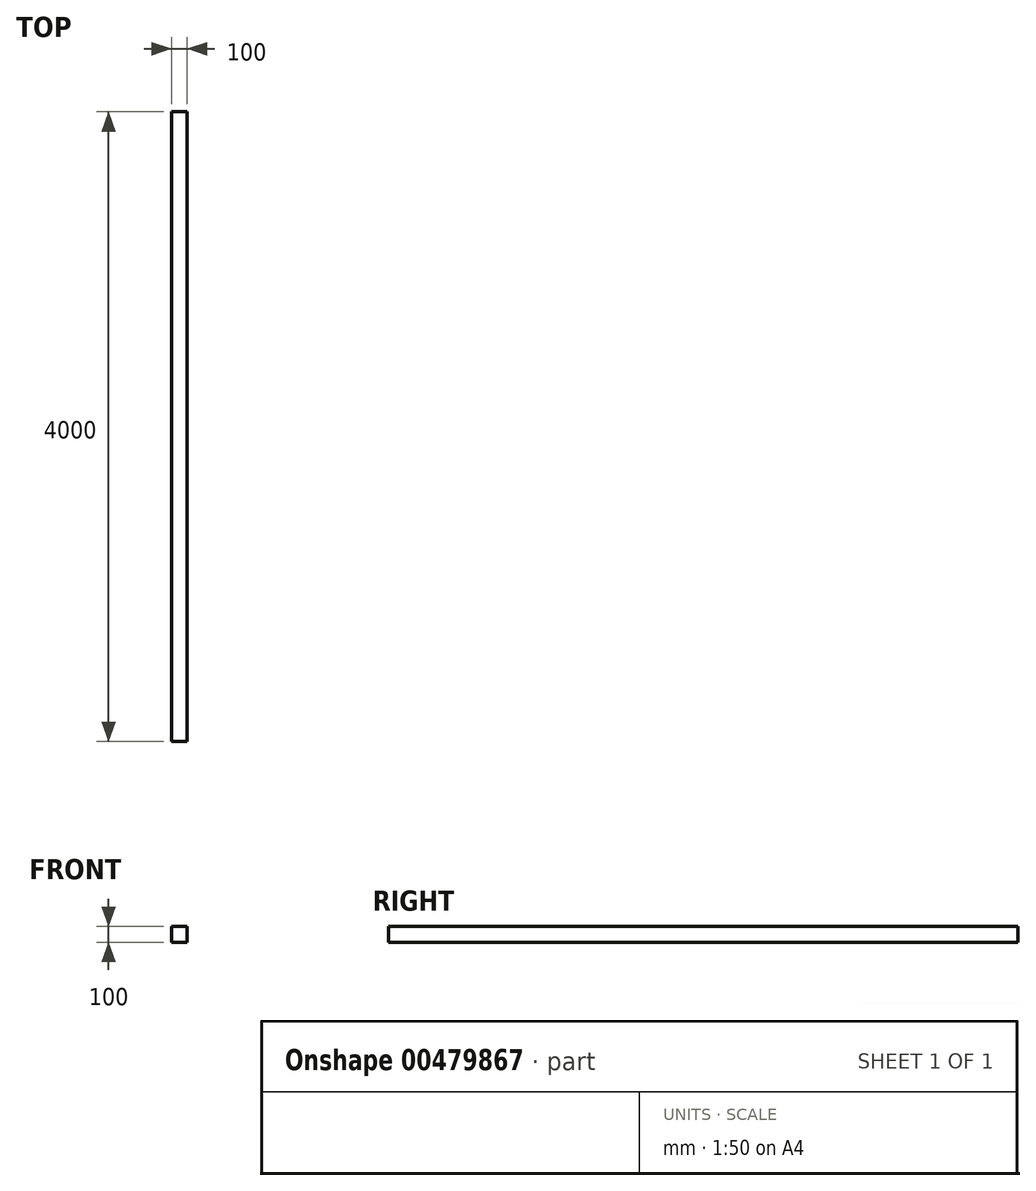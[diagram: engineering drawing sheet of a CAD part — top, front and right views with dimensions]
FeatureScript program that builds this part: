
annotation { "Feature Type Name" : "Feature", "Feature Type Description" : "" }
export const myFeature = defineFeature(function(context is Context, id is Id, definition is map)
    precondition{}
    {
        {
            var Q0;
            Q0=qCreatedBy(makeId("Right.planeOp"),FACE);
            var sketch = newSketch(context, id + "F0", { "sketchPlane" : qUnion([Q0])});
            skLineSegment(sketch, "E0", {"start": v(0, 0) * mm, "end": v(0, -100) * mm});
            skLineSegment(sketch, "E1", {"start": v(0, -100) * mm, "end": v(-4000, -100) * mm});
            skLineSegment(sketch, "E2", {"start": v(-4000, -100) * mm, "end": v(-4000, 0) * mm});
            skLineSegment(sketch, "E3", {"start": v(-4000, 0) * mm, "end": v(0, 0) * mm});
            skSolve(sketch);
        }
        {
            var Q0;
            Q0=makeQuery(id+"F0.imprint","IMPRINT",FACE,{"disambiguationData":[TD([[makeQuery(id+"F0.imprint","IMPRINT",EDGE,{"derivedFrom":sQuery(id+"F0.wireOp",EDGE,"E0")}),-1.0]])]});
            extrude(context, id + "F1", {"entities" : qUnion([Q0]), "depth" : 100 * mm});
        }
    });
